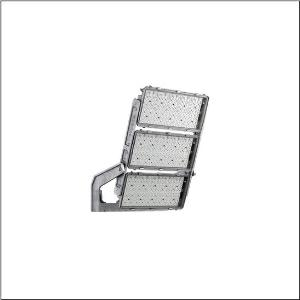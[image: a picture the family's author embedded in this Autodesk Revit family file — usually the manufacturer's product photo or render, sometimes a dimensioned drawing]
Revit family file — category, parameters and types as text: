
# Revit family: floodlight_fl_11_maxi_pro_remote___pl33t_5xa779427t01aa_b0c2
name_source: partatom
category: Lighting Fixtures
units: mm (PartAtom-declared; Revit-internal decimal feet)

## family parameters
Cut with Voids When Loaded = No
Host = Face
Light Source = No
Part Type = Normal
Room Calculation Point = No
Round Connector Dimension = Use Diameter
Shared = No

## types (1)
- --- (1 x LED, 215350 lm, 1540.1 W, 5000K)
    Apparent Load = 1540 VA
    CIE Flux Codes = 27 70 98 100 100
    Color Rendering = 70
    Color Temperature = 5000K
    Default Elevation = 1800 mm
    Description = Floodlight FL 11  maxi  pro Remote floodlight; light control with lens of PMMA; cover panel of toughened safety glass, transparent; light distribution: PL33T, asymmetric direct distribution, LEDcolour temperature: 5000K, rated luminous flux: 215.350lm, colour rendering: CRI > 70, light colour: 750; luminous efficacy: 140lm/W; brightness control: DALI 2 (1 DALI address); with terminal, 8-pole, max. 2.5mm², mains connection: 220..240V/380..400V AC, 50/60Hz, surge voltage resistance: line to ground: 10kV, ECG replaceable separately, no afterglow with DALI off / DMX off command, LED unit replaceable without ESD environment, dustproof LED module, dimming range 10..100%; 1540W floodlight with 2x LED unit of diecast aluminium, coated grey; length: 713mm / width: 651mm / height: 338mm; mounting bracket, of diecast aluminium, uncoated, natural, equipment: Power, protection rating (complete): IP66; insulation class (complete): insulation class I (protective earthing); certification: CE, ENEC, VDE; ball protection: ball impact resistance with accessories, impact resistance: IK07; only for outdoor installations, rated ambient temperature 10°C, permissible operating ambient temperature: -40..+30°C, permissible storage temperature: -40..+85°C; packaging unit: 1 piece

Light Distribution: PL33T
    Height = 320 mm
    Lamp = 1 x LED
    Lamp Light Flux = 215350 lm
    Lamp Power = 1540.1 W
    Lamp count = 1
    Length = 1002 mm
    Luminous efficacy = 140 lm/W
    Manufacturer = Siteco
    ModVariant = No
    Model = 5XA779427T01AA
    Mounting Place = Ceiling
    Mounting Type = Surface mounted
    Number of Poles = 1
    OnlyDefault = Yes
    Power Factor = 1
    Product Name = Floodlight FL 11 maxi pro Remote | PL33T
    Product group = floodlight | ceiling mounted
    ProductGroupID = 302
    Protection Class = Protection class I
    Protection Degree = IP 66
    RLX_Detail_Level = 1
    RLX_Emergency_Light_Flux = 0 lm
    RLX_Emergency_Type = 0
    RLX_Emergency_Type_DB = No
    RlxData = <blob elided: 52521 chars, md5=446df52b>
    Socket = socket
    Standby Power = 0 W
    System Light Flux = 215350 lm
    System Power = 1540 W
    Type Comments = factory setting: luminous flux: 100 % | dim-lin: 254 | 1080 mA
    Type Image = l_1006784.jpg
    URL = http://relux.com
    VarID = @adj_048779
    Voltage = 0 V
    Weight = 0.00 kg
    Width = 655 mm

## geometry (parser evidence)
native form markers: Blend x4, Sweep x12
no freeform markers — native parametric forms only
